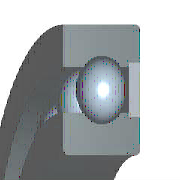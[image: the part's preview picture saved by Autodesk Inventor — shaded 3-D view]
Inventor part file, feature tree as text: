
AUTODESK INVENTOR PART (.ipt)
format: ipt  version: 2019 (Build 230136000, 136)  size: 315,392 bytes
history: native  units: mm (DEFAULTED — no unit token found)
features: sketch x1, other x1, pattern_circular x1
ambient origin geometry x8: Origin, YZ Plane, XZ Plane, XY Plane, X Axis, Y Axis, Z Axis, Center Point
bodies: Solid1 (feature_tree), Body (feature_tree)
feature tree (3):
  sketch  "Sketch"  dims[d0=4.16mm d17=90.0deg d18=90.0deg d1=0.3mm d2=70.0mm d3=360.0deg d4=0.0mm d5=0.0mm d6=0.0mm d7=10.0mm d8=26.0mm d9=18.0mm d10=26.0mm d11=15.216mm d12=14.4552mm d13=15.216mm d14=0.0mm d15=6.666667mm d16=8.0mm d19=1.333333mm d20=2.666667mm d22=4.0mm d23=0.0mm d24=0.0mm]
  other  "Ball"
  pattern_circular  "Balls"  Angle=90.0deg  [1 undecoded]
note: 1 required parameter value undecoded (feature->parameter linkage not recoverable at this tier; creation-order binding heuristic only, values carry confidence <= 0.55)
